# Revit family: Connected_Backflow_w-Wireless_Monitor_Zurn_Wilkins-Model_375W1 (212-10_Inch)
name_source: partatom
category: Pipe Accessories
units: mm (PartAtom-declared; Revit-internal decimal feet)

## family parameters
Always vertical = Yes
Cut with Voids When Loaded = No
OmniClass Number = 23.65.55.14.21
OmniClass Title = Non-Return Valves for Liquid Services
Part Type = Valve - Breaks Into
Round Connector Dimension = Use Radius
Shared = No
Work Plane-Based = No

## types (6) — shared parameters
Assembly Code = D2020300
Default Elevation = 0' - 0"
Description = Reduced Pressure Principle Assembly with Integral Relief Valve Monitor
Flow Rate (GPM) = 0 GPM
Height = 1' - 0"
Hydrostatic Test Pressure = 350.00 psi
Length = 2' - 0"
Main Material = Paint - Zurn - Ductile Iron - Blue
Manufacturer = Zurn Water, LLC
Manufacturer Brand = Zurn Wilkins
Max Working Water Pressure = 175.00 psi
Max Working Water Temperature = 140 °F
Model = 375W1
Modified Date = 09/08/2025
Product Documentation Link = https://files.zurn.com
Product Installation Sheet URL = https://files.zurn.com
Product Page URL = https://www.zurn.com
Product data URL = https://www.bimobject.com
Repair Parts URL = https://files.zurn.com
URL = www.zurn.com
Width = 1' - 0"

## per-type parameters (varying)
- 212-375W1 (2-1/2" 375W1): Body Length=0' - 5 9/16"; Body Location=0' - 6 1/32"; Body Radius=0' - 2 13/16"; Body Radius_Masking=0' - 2 13/16"; Centre=0' - 7 15/16"; Control Box=BF_Control_Box-Valve_Mounted : 212-375; Coupling Radius=0' - 3 1/2"; Coupling width=0' - 1 13/16"; DIM A Total Length=2' - 7"; DIM B - MAIN VALVE BODY LENGTH=1' - 3 7/8"; DIM C Center to ball valve End=0' - 7 1/4"; DIM D center to left end=0' - 3 3/4"; DIM E Center to top=2' - 2 1/8"; DIM F - VALVE CENTER TO RELIEF VALVE BOTTOM=0' - 9 1/2"; DIM G - MAIN VALVE BODY LEFT END TO RELIEF VALVE OUTLET CENTER=0' - 8 3/8"; Flange Radius=0' - 3 1/2"; Flange Radius_Masking=0' - 3 1/2"; Flange Thickness=0' - 0 11/16"; Gate Valve with Test Cock=Gate_Valve-Zurn_Wilkins-Model_48_Flanged_Test_Cock_1-(212-10_Inch) : 2 1/2"; Gate valve=Gate_Valve-Zurn_Wilkins-Model_48_Flanged-(2.5-10_Inch) : 2 1/2"; Main Body=Main_Body_375W1_(212-10_Inch) : 212-375W1 (2-1/2" 375W1 Body); Mid plane=1' - 3 1/2"; Nominal Diameter=0' - 2 1/2"; Nominal Radius=0' - 1 1/4"; Pipe Radius=0' - 1 1/4"; Pipe Radius_Masking=0' - 1 1/4"; Pressure Loss at Rated Flow=14.00 psi; Product Weight (lbs)=167; Rated Flow=220 GPM; Ref D=0' - 1 13/16"; Ref D_Masking=0' - 1 13/16"; Ref E=0' - 1"; Ref F=0' - 1"; Ref G=25.00°; Ref H=25.00°; Ref H_Masking=0' - 3 1/2"; Tailpiece Angle=135.00°; Tailpiece Location=0' - 5 9/16"; Tailpiece Width=0' - 1 19/32"; Test Cock 2 Height=0' - 5"; Test Cock Height=0' - 6"; Test cock 3 Height=0' - 3 7/16"; Tubing Location=0' - 1 5/8"
- 3-375W1 (3" 375W1): Body Length=0' - 5 9/16"; Body Location=0' - 6 1/32"; Body Radius=0' - 3 3/16"; Body Radius_Masking=0' - 3 3/16"; Centre=0' - 7 15/16"; Control Box=BF_Control_Box-Valve_Mounted : 3-375; Coupling Radius=0' - 3 1/2"; Coupling width=0' - 1 13/16"; DIM A Total Length=2' - 8"; DIM B - MAIN VALVE BODY LENGTH=1' - 3 7/8"; DIM C Center to ball valve End=0' - 7 1/4"; DIM D center to left end=0' - 3 3/4"; DIM E Center to top=2' - 2 5/16"; DIM F - VALVE CENTER TO RELIEF VALVE BOTTOM=0' - 9 1/2"; DIM G - MAIN VALVE BODY LEFT END TO RELIEF VALVE OUTLET CENTER=0' - 8 3/8"; Flange Radius=0' - 3 3/4"; Flange Radius_Masking=0' - 3 3/4"; Flange Thickness=0' - 0 11/16"; Gate Valve with Test Cock=Gate_Valve-Zurn_Wilkins-Model_48_Flanged_Test_Cock_1-(212-10_Inch) : 3"; Gate valve=Gate_Valve-Zurn_Wilkins-Model_48_Flanged-(2.5-10_Inch) : 3"; Main Body=Main_Body_375W1_(212-10_Inch) : 3-375W1 (3" 375W1 Body); Mid plane=1' - 4"; Nominal Diameter=0' - 3"; Nominal Radius=0' - 1 1/2"; Pipe Radius=0' - 1 1/2"; Pipe Radius_Masking=0' - 1 1/2"; Pressure Loss at Rated Flow=15.00 psi; Product Weight (lbs)=189; Rated Flow=310 GPM; Ref D=0' - 2 3/16"; Ref D_Masking=0' - 2 3/16"; Ref E=0' - 1"; Ref F=0' - 1"; Ref G=25.00°; Ref H=25.00°; Ref H_Masking=0' - 3 1/2"; Tailpiece Angle=135.00°; Tailpiece Location=0' - 5 9/16"; Tailpiece Width=0' - 1 19/32"; Test Cock 2 Height=0' - 5 1/2"; Test Cock Height=0' - 6 1/2"; Test cock 3 Height=0' - 3 13/16"; Tubing Location=0' - 1 5/8"
- 4-375W1 (4" 375W1): Body Length=0' - 6 13/16"; Body Location=0' - 7 13/32"; Body Radius=0' - 3 3/16"; Body Radius_Masking=0' - 3 3/16"; Centre=0' - 9 3/4"; Control Box=BF_Control_Box-Valve_Mounted : 4-375; Coupling Radius=0' - 4"; Coupling width=0' - 2"; DIM A Total Length=3' - 1 5/8"; DIM B - MAIN VALVE BODY LENGTH=1' - 7 1/2"; DIM C Center to ball valve End=0' - 8"; DIM D center to left end=0' - 4 15/16"; DIM E Center to top=2' - 2 1/2"; DIM F - VALVE CENTER TO RELIEF VALVE BOTTOM=0' - 11"; DIM G - MAIN VALVE BODY LEFT END TO RELIEF VALVE OUTLET CENTER=0' - 9 1/4"; Flange Radius=0' - 4 1/2"; Flange Radius_Masking=0' - 4 1/2"; Flange Thickness=0' - 0 11/16"; Gate Valve with Test Cock=Gate_Valve-Zurn_Wilkins-Model_48_Flanged_Test_Cock_1-(212-10_Inch) : 4"; Gate valve=Gate_Valve-Zurn_Wilkins-Model_48_Flanged-(2.5-10_Inch) : 4"; Main Body=Main_Body_375W1_(212-10_Inch) : 4-375W1 (4" 375W1 Body); Mid plane=1' - 6 13/16"; Nominal Diameter=0' - 4"; Nominal Radius=0' - 2"; Pipe Radius=0' - 2"; Pipe Radius_Masking=0' - 2"; Pressure Loss at Rated Flow=9.00 psi; Product Weight (lbs)=283; Rated Flow=500 GPM; Ref D=0' - 2 3/16"; Ref D_Masking=0' - 2 3/16"; Ref E=0' - 1 1/4"; Ref F=0' - 1 1/2"; Ref G=35.00°; Ref H=35.00°; Ref H_Masking=0' - 4"; Tailpiece Angle=135.00°; Tailpiece Location=0' - 6 13/16"; Tailpiece Width=0' - 1 15/16"; Test Cock 2 Height=0' - 5 1/2"; Test Cock Height=0' - 7"; Test cock 3 Height=0' - 4 5/16"; Tubing Location=0' - 2"
- 6-375W1 (6" 375W1): Body Length=0' - 8 7/32"; Body Location=0' - 8 15/16"; Body Radius=0' - 5 9/32"; Body Radius_Masking=0' - 5 9/32"; Centre=0' - 11 3/4"; Control Box=BF_Control_Box-Valve_Mounted : 6-375; Coupling Radius=0' - 5 9/32"; Coupling width=0' - 2"; DIM A Total Length=3' - 8 3/4"; DIM B - MAIN VALVE BODY LENGTH=1' - 11 1/2"; DIM C Center to ball valve End=0' - 10"; DIM D center to left end=0' - 6 5/16"; DIM E Center to top=2' - 6 1/2"; DIM F - VALVE CENTER TO RELIEF VALVE BOTTOM=1' - 0 3/8"; DIM G - MAIN VALVE BODY LEFT END TO RELIEF VALVE OUTLET CENTER=0' - 10 3/4"; Flange Radius=0' - 5 1/2"; Flange Radius_Masking=0' - 5 1/2"; Flange Thickness=0' - 1"; Gate Valve with Test Cock=Gate_Valve-Zurn_Wilkins-Model_48_Flanged_Test_Cock_1-(212-10_Inch) : 6"; Gate valve=Gate_Valve-Zurn_Wilkins-Model_48_Flanged-(2.5-10_Inch) : 6"; Main Body=Main_Body_375W1_(212-10_Inch) : 6-375W1 (6" 375W1 Body); Mid plane=1' - 10 3/8"; Nominal Diameter=0' - 6"; Nominal Radius=0' - 3"; Pipe Radius=0' - 3"; Pipe Radius_Masking=0' - 3"; Pressure Loss at Rated Flow=9.00 psi; Product Weight (lbs)=464; Rated Flow=1000 GPM; Ref D=0' - 4 9/32"; Ref D_Masking=0' - 4 9/32"; Ref E=0' - 1 1/2"; Ref F=0' - 2"; Ref G=45.00°; Ref H=35.00°; Ref H_Masking=0' - 5 9/32"; Tailpiece Angle=135.00°; Tailpiece Location=0' - 8 7/32"; Tailpiece Width=0' - 2 11/32"; Test Cock 2 Height=0' - 7 1/2"; Test Cock Height=0' - 9 1/2"; Test cock 3 Height=0' - 5 7/32"; Tubing Location=0' - 2 1/8"
- 8-375W1 (8" 375W1): Body Length=1' - 1 7/32"; Body Location=1' - 2 11/32"; Body Radius=0' - 7 3/16"; Body Radius_Masking=0' - 7 3/16"; Centre=1' - 6 7/8"; Control Box=BF_Control_Box-Valve_Mounted : 8-375; Coupling Radius=0' - 7 1/2"; Coupling width=0' - 2 1/2"; DIM A Total Length=5' - 0 3/4"; DIM B - MAIN VALVE BODY LENGTH=3' - 1 3/4"; DIM C Center to ball valve End=0' - 11"; DIM D center to left end=0' - 9"; DIM E Center to top=2' - 10 1/2"; DIM F - VALVE CENTER TO RELIEF VALVE BOTTOM=1' - 3 3/8"; DIM G - MAIN VALVE BODY LEFT END TO RELIEF VALVE OUTLET CENTER=1' - 4 3/4"; Flange Radius=0' - 6 3/4"; Flange Radius_Masking=0' - 6 3/4"; Flange Thickness=0' - 1"; Gate Valve with Test Cock=Gate_Valve-Zurn_Wilkins-Model_48_Flanged_Test_Cock_1-(212-10_Inch) : 8"; Gate valve=Gate_Valve-Zurn_Wilkins-Model_48_Flanged-(2.5-10_Inch) : 8"; Main Body=Main_Body_375W1_(212-10_Inch) : 8-375W1 (8" 375W1 Body); Mid plane=2' - 6 3/8"; Nominal Diameter=0' - 8"; Nominal Radius=0' - 4"; Pipe Radius=0' - 4"; Pipe Radius_Masking=0' - 4"; Pressure Loss at Rated Flow=10.00 psi; Product Weight (lbs)=834; Rated Flow=1600 GPM; Ref D=0' - 6 3/16"; Ref D_Masking=0' - 6 3/16"; Ref E=0' - 2"; Ref F=0' - 2 1/2"; Ref G=45.00°; Ref H=45.00°; Ref H_Masking=0' - 7 1/2"; Tailpiece Angle=145.00°; Tailpiece Location=1' - 1 7/32"; Tailpiece Width=0' - 3 25/32"; Test Cock 2 Height=0' - 10"; Test Cock Height=1' - 0 1/2"; Test cock 3 Height=0' - 6 13/16"; Tubing Location=0' - 2 1/2"
- 10-375W1 (10" 375W1): Body Length=1' - 1 7/32"; Body Location=1' - 2 11/32"; Body Radius=0' - 7 3/16"; Body Radius_Masking=0' - 7 3/16"; Centre=1' - 6 7/8"; Control Box=BF_Control_Box-Valve_Mounted : 10-375; Coupling Radius=0' - 7 1/2"; Coupling width=0' - 2 1/2"; DIM A Total Length=5' - 3 3/4"; DIM B - MAIN VALVE BODY LENGTH=3' - 1 3/4"; DIM C Center to ball valve End=0' - 11"; DIM D center to left end=0' - 9"; DIM E Center to top=2' - 10 3/4"; DIM F - VALVE CENTER TO RELIEF VALVE BOTTOM=1' - 3 3/8"; DIM G - MAIN VALVE BODY LEFT END TO RELIEF VALVE OUTLET CENTER=1' - 4 3/4"; Flange Radius=0' - 8"; Flange Radius_Masking=0' - 8"; Flange Thickness=0' - 1 3/16"; Gate Valve with Test Cock=Gate_Valve-Zurn_Wilkins-Model_48_Flanged_Test_Cock_1-(212-10_Inch) : 10"; Gate valve=Gate_Valve-Zurn_Wilkins-Model_48_Flanged-(2.5-10_Inch) : 10"; Main Body=Main_Body_375W1_(212-10_Inch) : 10-375W1 (10" 375W1 Body); Mid plane=2' - 7 7/8"; Nominal Diameter=0' - 10"; Nominal Radius=0' - 5"; Pipe Radius=0' - 5"; Pipe Radius_Masking=0' - 5"; Pressure Loss at Rated Flow=12.00 psi; Product Weight (lbs)=1172; Rated Flow=2300 GPM; Ref D=0' - 6 3/16"; Ref D_Masking=0' - 6 3/16"; Ref E=0' - 2"; Ref F=0' - 2 1/2"; Ref G=45.00°; Ref H=45.00°; Ref H_Masking=0' - 7 1/2"; Tailpiece Angle=145.00°; Tailpiece Location=1' - 1 7/32"; Tailpiece Width=0' - 3 25/32"; Test Cock 2 Height=0' - 10 1/2"; Test Cock Height=1' - 1"; Test cock 3 Height=0' - 8 5/16"; Tubing Location=0' - 3"

## geometry (parser evidence)
native form markers: Sweep x12
no freeform markers — native parametric forms only
